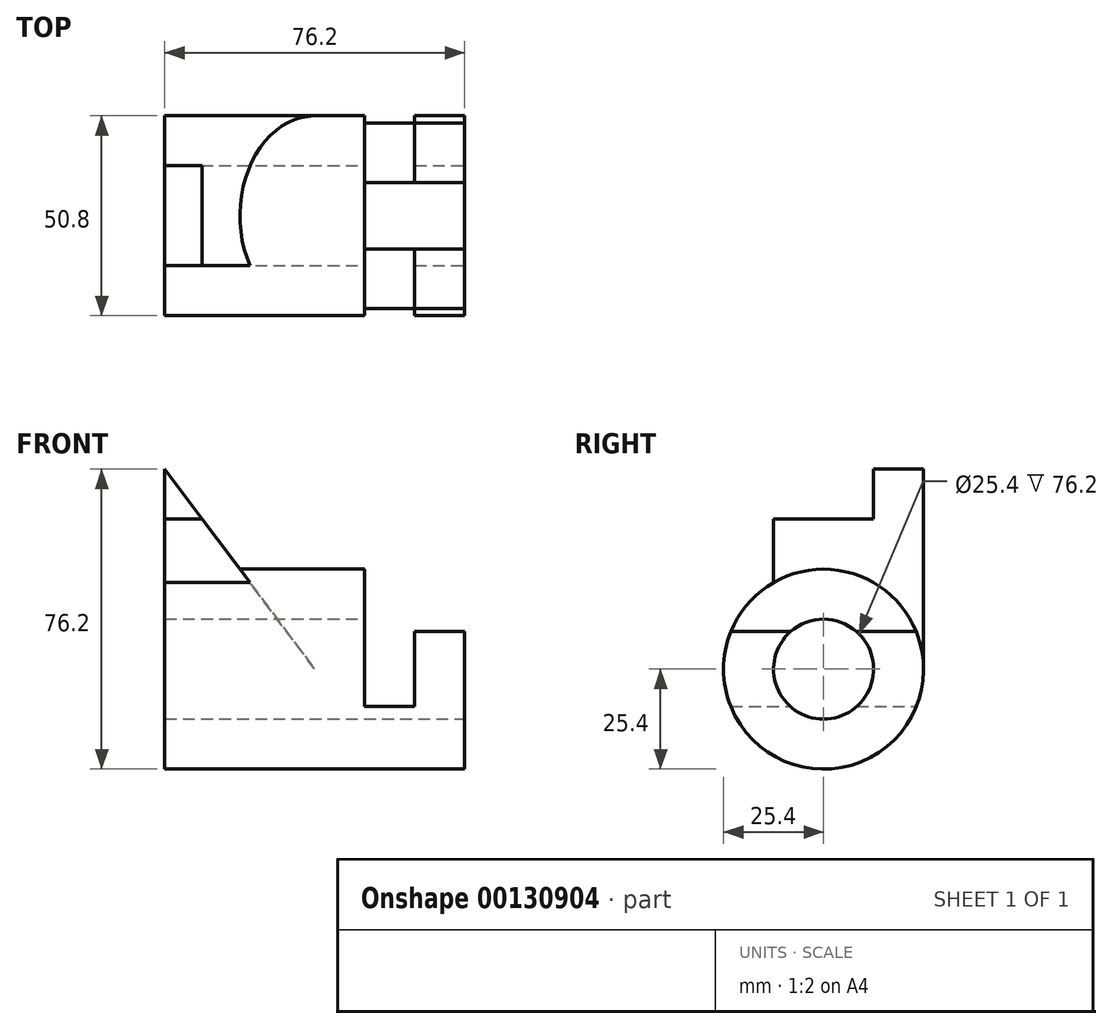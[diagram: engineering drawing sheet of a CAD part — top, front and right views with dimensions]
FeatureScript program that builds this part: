
annotation { "Feature Type Name" : "Feature", "Feature Type Description" : "" }
export const myFeature = defineFeature(function(context is Context, id is Id, definition is map)
    precondition{}
    {
        {
            var Q0;
            Q0=qCreatedBy(makeId("Right.planeOp"),FACE);
            var sketch = newSketch(context, id + "F0", { "sketchPlane" : qUnion([Q0])});
            skLineSegment(sketch, "E0", {"start": v(0, 0) * mm, "end": v(0, 50.8) * mm});
            skLineSegment(sketch, "E1", {"start": v(0, 50.8) * mm, "end": v(-12.7, 50.8) * mm});
            skLineSegment(sketch, "E2", {"start": v(-12.7, 50.8) * mm, "end": v(-12.7, 38.1) * mm});
            skLineSegment(sketch, "E3", {"start": v(-12.7, 38.1) * mm, "end": v(-38.1, 38.1) * mm});
            skLineSegment(sketch, "E4", {"start": v(-38.1, 38.1) * mm, "end": v(-38.1, 0) * mm});
            skLineSegment(sketch, "E5", {"start": v(-38.1, 0) * mm, "end": v(0, 0) * mm});
            skSolve(sketch);
        }
        {
            var Q0;
            Q0=qSketchRegion(id+"F0",true);
            extrude(context, id + "F1", {"entities" : qUnion([Q0]), "oppositeDirection" : true, "depth" : 38.1 * mm});
        }
        {
            var Q0;
            Q0=qCreatedBy(makeId("Front.planeOp"),FACE);
            var sketch = newSketch(context, id + "F2", { "sketchPlane" : qUnion([Q0])});
            skLineSegment(sketch, "E6", {"start": v(0, 0) * mm, "end": v(-38.1, 50.8) * mm});
            skLineSegment(sketch, "E7", {"start": v(-38.1, 50.8) * mm, "end": v(0, 50.8) * mm});
            skLineSegment(sketch, "E8", {"start": v(0, 50.8) * mm, "end": v(0, 0) * mm});
            skSolve(sketch);
        }
        {
            var Q0;
            Q0=qSketchRegion(id+"F2",true);
            extrude(context, id + "F3", {"entities" : qUnion([Q0]), "operationType" : NewBodyOperationType.REMOVE, "endBound" : BoundingType.THROUGH_ALL, "depth" : 25.4 * mm});
        }
        {
            var Q0;
            Q0=qCreatedBy(makeId("Right.planeOp"),FACE);
            cPlane(context, id + "F4", {"entities" : qUnion([Q0]), "cplaneType" : CPlaneType.OFFSET, "offset" : 12.7 * mm, "width" : 152.4 * mm, "height" : 152.4 * mm});
        }
        {
            var Q0;
            Q0=qCreatedBy(id+"F4.planeOp",FACE);
            var sketch = newSketch(context, id + "F5", { "sketchPlane" : qUnion([Q0])});
            skLineSegment(sketch, "E9", {"start": v(0, 0) * mm, "end": v(-25.4, 0) * mm, "construction": true});
            skCircle(sketch, "E10", {"center": v(-25.4, 0) * mm, "radius": 25.4 * mm});
            skSolve(sketch);
        }
        {
            var Q0;
            Q0=qSketchRegion(id+"F5",true);
            extrude(context, id + "F6", {"entities" : qUnion([Q0]), "operationType" : NewBodyOperationType.ADD, "oppositeDirection" : true, "depth" : 50.8 * mm});
        }
        {
            var Q0;
            Q0=makeQuery(id+"F6.opExtrude","CAP_FACE",FACE,{"disambiguationData":[OSD([sQuery(id+"F5.wireOp",EDGE,"E10")])],"isStart":true});
            extrude(context, id + "F7", {"entities" : qUnion([Q0]), "operationType" : NewBodyOperationType.ADD, "depth" : 25.4 * mm});
        }
        {
            var Q0;
            Q0=makeQuery(id+"F7.opExtrude","CAP_FACE",FACE,{"disambiguationData":[OSD([sQuery(id+"F5.wireOp",EDGE,"E10")])],"isStart":false});
            var sketch = newSketch(context, id + "F8", { "sketchPlane" : qUnion([Q0])});
            skCircle(sketch, "E11", {"center": v(-25.4, 0) * mm, "radius": 12.7 * mm});
            skSolve(sketch);
        }
        {
            var Q0;
            Q0=qSketchRegion(id+"F8",true);
            extrude(context, id + "F9", {"entities" : qUnion([Q0]), "operationType" : NewBodyOperationType.REMOVE, "endBound" : BoundingType.THROUGH_ALL, "oppositeDirection" : true, "depth" : 25.4 * mm});
        }
        {
            var Q0;
            Q0=qCreatedBy(makeId("Front.planeOp"),FACE);
            var sketch = newSketch(context, id + "F10", { "sketchPlane" : qUnion([Q0])});
            skLineSegment(sketch, "E12", {"start": v(38.1, 25.4) * mm, "end": v(38.1, 9.53) * mm});
            skLineSegment(sketch, "E13", {"start": v(38.1, 9.53) * mm, "end": v(25.4, 9.52) * mm});
            skLineSegment(sketch, "E14", {"start": v(25.4, 9.52) * mm, "end": v(25.4, -9.52) * mm});
            skLineSegment(sketch, "E15", {"start": v(25.4, -9.52) * mm, "end": v(12.7, -9.52) * mm});
            skLineSegment(sketch, "E16", {"start": v(12.7, -9.52) * mm, "end": v(12.7, 25.4) * mm});
            skLineSegment(sketch, "E17", {"start": v(12.7, 25.4) * mm, "end": v(12.7, 0) * mm});
            skLineSegment(sketch, "E18", {"start": v(12.7, 0) * mm, "end": v(12.7, -9.52) * mm});
            skLineSegment(sketch, "E19", {"start": v(12.7, 25.4) * mm, "end": v(38.1, 25.4) * mm});
            skSolve(sketch);
        }
        {
            var Q0;
            Q0=qSketchRegion(id+"F10",true);
            extrude(context, id + "F11", {"entities" : qUnion([Q0]), "operationType" : NewBodyOperationType.REMOVE, "endBound" : BoundingType.THROUGH_ALL, "depth" : 25.4 * mm});
        }
    });
